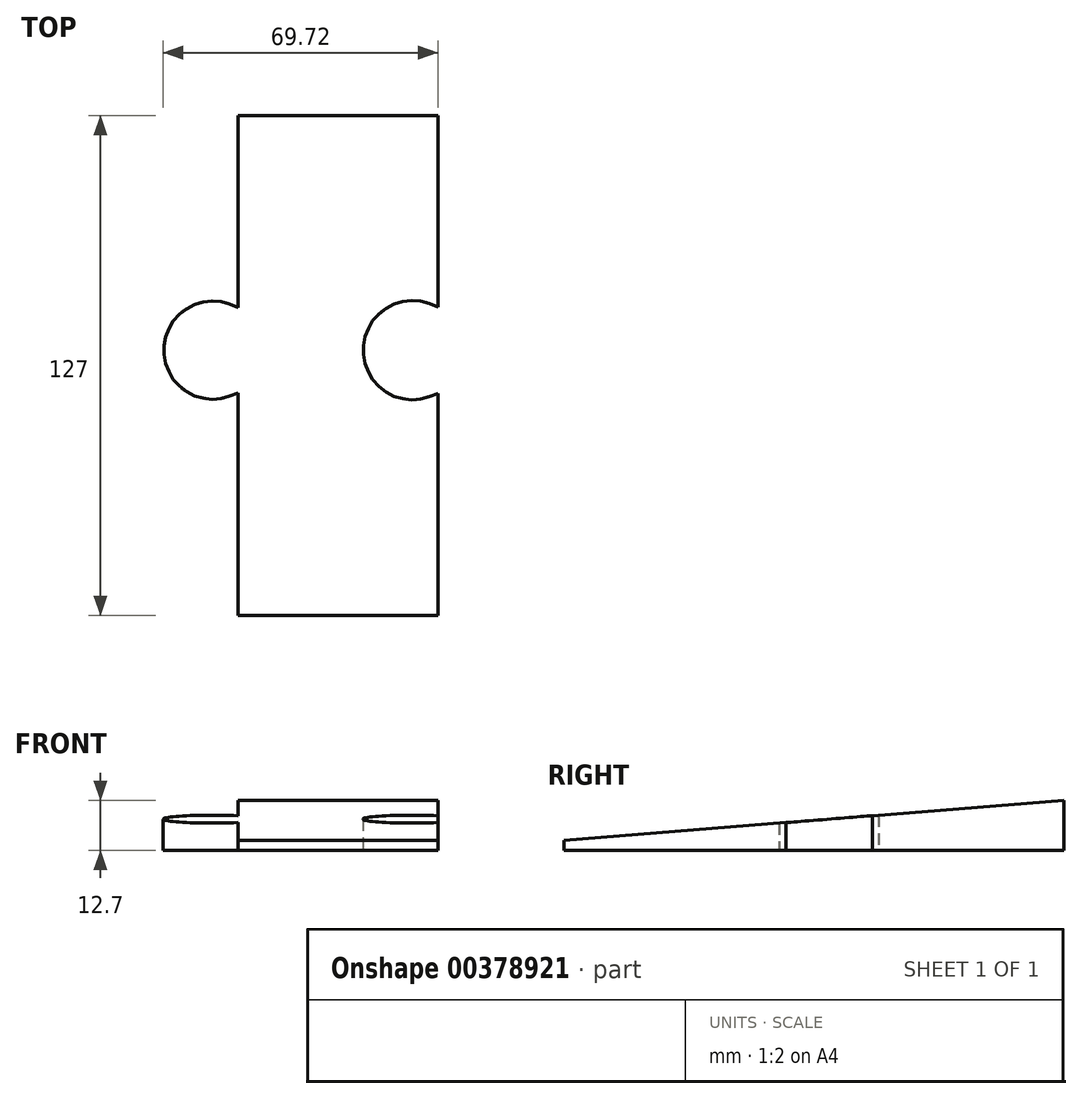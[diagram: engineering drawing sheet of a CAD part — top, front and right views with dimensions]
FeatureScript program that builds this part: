
annotation { "Feature Type Name" : "Feature", "Feature Type Description" : "" }
export const myFeature = defineFeature(function(context is Context, id is Id, definition is map)
    precondition{}
    {
        {
            var Q0;
            Q0=qCreatedBy(makeId("Right.planeOp"),FACE);
            var sketch = newSketch(context, id + "F0", { "sketchPlane" : qUnion([Q0])});
            skLineSegment(sketch, "E0", {"start": v(-67.39, 0) * mm, "end": v(-67.39, 2.54) * mm});
            skLineSegment(sketch, "E1", {"start": v(-67.39, 2.54) * mm, "end": v(59.61, 12.7) * mm});
            skLineSegment(sketch, "E2", {"start": v(59.61, 12.7) * mm, "end": v(59.61, 0) * mm});
            skLineSegment(sketch, "E3", {"start": v(59.61, 0) * mm, "end": v(-67.39, 0) * mm});
            skSolve(sketch);
        }
        {
            var Q0;
            Q0=makeQuery(id+"F0.imprint","IMPRINT",FACE,{"disambiguationData":[TD([[makeQuery(id+"F0.imprint","IMPRINT",EDGE,{"derivedFrom":sQuery(id+"F0.wireOp",EDGE,"E0")}),-1.0]])]});
            extrude(context, id + "F1", {"entities" : qUnion([Q0]), "endBound" : BoundingType.SYMMETRIC, "depth" : 50.8 * mm});
        }
        {
            var Q0;
            Q0=qCreatedBy(makeId("Top.planeOp"),FACE);
            var sketch = newSketch(context, id + "F2", { "sketchPlane" : qUnion([Q0])});
            skCircle(sketch, "E4", {"center": v(19.05, 0) * mm, "radius": 12.7 * mm});
            skCircle(sketch, "E5", {"center": v(-31.75, 0) * mm, "radius": 12.7 * mm});
            skSolve(sketch);
        }
        {
            var Q0;
            Q0=makeQuery(id+"F2.imprint","IMPRINT",FACE,{"disambiguationData":[TD([[makeQuery(id+"F2.imprint","IMPRINT",EDGE,{"derivedFrom":sQuery(id+"F2.wireOp",EDGE,"E4")}),1.0]])]});
            extrude(context, id + "F3", {"entities" : qUnion([Q0]), "operationType" : NewBodyOperationType.REMOVE, "depth" : 25.4 * mm});
        }
        {
            var Q0;
            Q0=makeQuery(id+"F2.imprint","IMPRINT",FACE,{"disambiguationData":[TD([[makeQuery(id+"F2.imprint","IMPRINT",EDGE,{"derivedFrom":sQuery(id+"F2.wireOp",EDGE,"E5")}),1.0]])]});
            var sketch = newSketch(context, id + "F4", { "sketchPlane" : qUnion([Q0])});
            skCircle(sketch, "E6.0", {"center": v(-31.75, 0) * mm, "radius": 12.57 * mm});
            skSolve(sketch);
        }
        {
            var Q0;
            Q0=makeQuery(id+"F4.imprint","IMPRINT",FACE,{"disambiguationData":[TD([[makeQuery(id+"F4.imprint","IMPRINT",EDGE,{"derivedFrom":sQuery(id+"F4.wireOp",EDGE,"E6.0")}),1.0]])]});
            var Q1;
            Q1=makeQuery(id+"F1.opExtrude","SWEPT_FACE",FACE,{"disambiguationData":[OSD([sQuery(id+"F0.wireOp",EDGE,"E1")])]});
            extrude(context, id + "F5", {"entities" : qUnion([Q0]), "operationType" : NewBodyOperationType.ADD, "endBound" : BoundingType.UP_TO_SURFACE, "endBoundEntityFace" : qUnion([Q1]), "depth" : 25.4 * mm});
        }
    });
